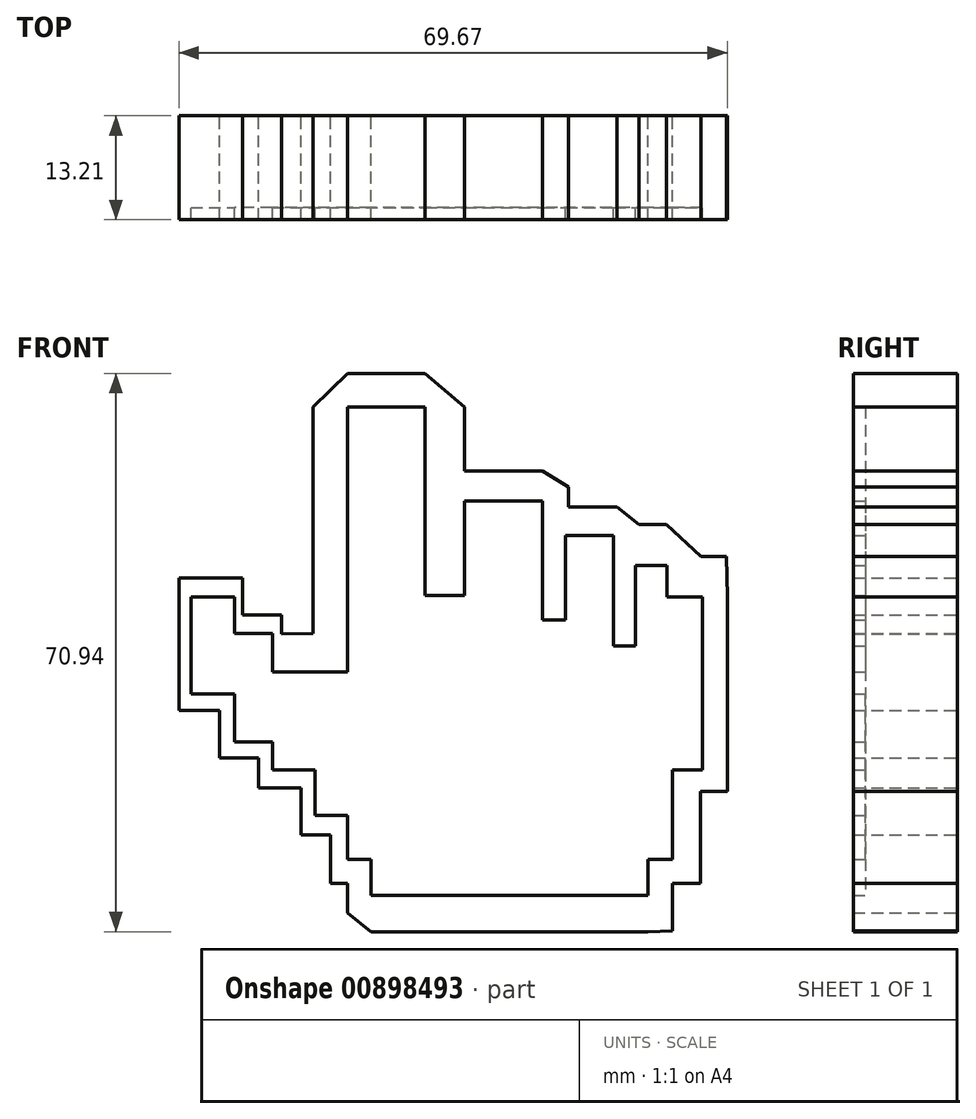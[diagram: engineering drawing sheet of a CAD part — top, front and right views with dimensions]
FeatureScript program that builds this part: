
annotation { "Feature Type Name" : "Feature", "Feature Type Description" : "" }
export const myFeature = defineFeature(function(context is Context, id is Id, definition is map)
    precondition{}
    {
        {
            var Q0;
            Q0=qCreatedBy(makeId("Front.planeOp"),FACE);
            var sketch = newSketch(context, id + "F0", { "sketchPlane" : qUnion([Q0])});
            skLineSegment(sketch, "E0.bottom", {"start": v(0, 0) * mm, "end": v(9.8, 0) * mm});
            skLineSegment(sketch, "E0.top", {"start": v(0, -4.26) * mm, "end": v(9.8, -4.26) * mm});
            skLineSegment(sketch, "E1.left", {"start": v(0, -4.26) * mm, "end": v(0, -28.2) * mm});
            skLineSegment(sketch, "E1.right", {"start": v(-4.42, -4.26) * mm, "end": v(-4.42, -28.2) * mm});
            skLineSegment(sketch, "E2.top", {"start": v(9.8, -28.2) * mm, "end": v(14.84, -28.2) * mm});
            skLineSegment(sketch, "E2.left", {"start": v(9.8, -4.26) * mm, "end": v(9.8, -28.2) * mm});
            skLineSegment(sketch, "E2.right", {"start": v(14.84, -4.26) * mm, "end": v(14.84, -12.42) * mm});
            skLineSegment(sketch, "E3.top", {"start": v(-4.42, -37.93) * mm, "end": v(0, -37.93) * mm});
            skLineSegment(sketch, "E3.left", {"start": v(-4.42, -28.2) * mm, "end": v(-4.42, -33.07) * mm});
            skLineSegment(sketch, "E3.right", {"start": v(0, -28.2) * mm, "end": v(0, -37.93) * mm});
            skLineSegment(sketch, "E4.bottom", {"start": v(14.84, -16.23) * mm, "end": v(24.73, -16.23) * mm});
            skLineSegment(sketch, "E4.top", {"start": v(14.84, -12.42) * mm, "end": v(24.73, -12.42) * mm});
            skLineSegment(sketch, "E5.top", {"start": v(27.68, -20.57) * mm, "end": v(33.76, -20.57) * mm});
            skLineSegment(sketch, "E5.left", {"start": v(24.73, -16.23) * mm, "end": v(24.73, -20.57) * mm});
            skLineSegment(sketch, "E6.top", {"start": v(36.54, -24.4) * mm, "end": v(40.53, -24.4) * mm});
            skLineSegment(sketch, "E6.left", {"start": v(33.76, -20.57) * mm, "end": v(33.76, -24.4) * mm});
            skLineSegment(sketch, "E7.top", {"start": v(40.53, -28.38) * mm, "end": v(45.04, -28.38) * mm});
            skLineSegment(sketch, "E7.left", {"start": v(40.53, -24.4) * mm, "end": v(40.53, -28.38) * mm});
            skLineSegment(sketch, "E8.top", {"start": v(24.73, -31.33) * mm, "end": v(27.68, -31.33) * mm});
            skLineSegment(sketch, "E8.left", {"start": v(24.73, -20.57) * mm, "end": v(24.73, -31.33) * mm});
            skLineSegment(sketch, "E8.right", {"start": v(27.68, -20.57) * mm, "end": v(27.68, -31.33) * mm});
            skLineSegment(sketch, "E9.top", {"start": v(33.76, -34.63) * mm, "end": v(36.54, -34.63) * mm});
            skLineSegment(sketch, "E9.left", {"start": v(33.76, -24.4) * mm, "end": v(33.76, -34.63) * mm});
            skLineSegment(sketch, "E9.right", {"start": v(36.54, -24.4) * mm, "end": v(36.54, -34.63) * mm});
            skLineSegment(sketch, "E10.left", {"start": v(45.04, -28.38) * mm, "end": v(45.04, -50.36) * mm});
            skLineSegment(sketch, "E10.right", {"start": v(48.22, -28.38) * mm, "end": v(48.22, -50.36) * mm});
            skLineSegment(sketch, "E11.bottom", {"start": v(45.04, -50.36) * mm, "end": v(41.22, -50.36) * mm});
            skLineSegment(sketch, "E11.right", {"start": v(41.22, -50.36) * mm, "end": v(41.22, -61.74) * mm});
            skLineSegment(sketch, "E12.bottom", {"start": v(41.22, -61.74) * mm, "end": v(38.15, -61.74) * mm});
            skLineSegment(sketch, "E12.right", {"start": v(38.15, -61.74) * mm, "end": v(38.15, -66.34) * mm});
            skLineSegment(sketch, "E13.bottom", {"start": v(38.15, -66.34) * mm, "end": v(2.98, -66.34) * mm});
            skLineSegment(sketch, "E13.top", {"start": v(38.15, -70.94) * mm, "end": v(2.98, -70.94) * mm});
            skLineSegment(sketch, "E14.top", {"start": v(2.98, -61.74) * mm, "end": v(0, -61.74) * mm});
            skLineSegment(sketch, "E14.left", {"start": v(2.98, -66.34) * mm, "end": v(2.98, -61.74) * mm});
            skLineSegment(sketch, "E15.top", {"start": v(0, -56.2) * mm, "end": v(-4.17, -56.2) * mm});
            skLineSegment(sketch, "E15.left", {"start": v(0, -61.74) * mm, "end": v(0, -56.2) * mm});
            skLineSegment(sketch, "E16.top", {"start": v(-4.17, -50.36) * mm, "end": v(-9.57, -50.36) * mm});
            skLineSegment(sketch, "E16.left", {"start": v(-4.17, -56.2) * mm, "end": v(-4.17, -50.36) * mm});
            skLineSegment(sketch, "E17.top", {"start": v(-9.57, -46.85) * mm, "end": v(-14.39, -46.85) * mm});
            skLineSegment(sketch, "E17.left", {"start": v(-9.57, -50.36) * mm, "end": v(-9.57, -46.85) * mm});
            skLineSegment(sketch, "E18.top", {"start": v(-14.39, -40.72) * mm, "end": v(-19.93, -40.72) * mm});
            skLineSegment(sketch, "E18.left", {"start": v(-14.39, -46.85) * mm, "end": v(-14.39, -40.72) * mm});
            skLineSegment(sketch, "E19.bottom", {"start": v(-19.93, -28.38) * mm, "end": v(-14.39, -28.38) * mm});
            skPoint(sketch, "E20.oppositeSnap0", {"position": v(-4.42, -33.07) * mm});
            skLineSegment(sketch, "E20.top", {"start": v(-14.39, -33.07) * mm, "end": v(-9.57, -33.07) * mm});
            skLineSegment(sketch, "E20.left", {"start": v(-14.39, -28.38) * mm, "end": v(-14.39, -33.07) * mm});
            skLineSegment(sketch, "E21.top", {"start": v(-9.57, -37.93) * mm, "end": v(-4.42, -37.93) * mm});
            skLineSegment(sketch, "E21.left", {"start": v(-9.57, -33.07) * mm, "end": v(-9.57, -37.93) * mm});
            skLineSegment(sketch, "E22", {"start": v(-19.93, -28.38) * mm, "end": v(-19.93, -40.72) * mm});
            skLineSegment(sketch, "E23", {"start": v(-4.42, -4.26) * mm, "end": v(0, 0) * mm});
            skLineSegment(sketch, "E24", {"start": v(9.8, 0) * mm, "end": v(14.84, -4.26) * mm});
            skLineSegment(sketch, "E25.trimOffspring", {"start": v(14.84, -16.23) * mm, "end": v(14.84, -28.2) * mm});
            skLineSegment(sketch, "E26", {"start": v(24.73, -12.42) * mm, "end": v(28.06, -14.42) * mm});
            skLineSegment(sketch, "E27", {"start": v(28.06, -14.42) * mm, "end": v(28.06, -17) * mm});
            skLineSegment(sketch, "E28", {"start": v(28.06, -17) * mm, "end": v(34.2, -17) * mm});
            skLineSegment(sketch, "E29", {"start": v(34.2, -17) * mm, "end": v(37.02, -19.21) * mm});
            skLineSegment(sketch, "E30", {"start": v(37.02, -19.21) * mm, "end": v(40.46, -19.21) * mm});
            skLineSegment(sketch, "E31", {"start": v(40.46, -19.21) * mm, "end": v(44.87, -23.26) * mm});
            skLineSegment(sketch, "E32", {"start": v(44.87, -23.26) * mm, "end": v(48.13, -23.26) * mm});
            skLineSegment(sketch, "E33", {"start": v(48.13, -23.26) * mm, "end": v(48.22, -28.38) * mm});
            skPoint(sketch, "E12.top.end.orphan", {"position": v(38.15, -70.94) * mm});
            skLineSegment(sketch, "E34", {"start": v(48.22, -50.36) * mm, "end": v(48.22, -53.11) * mm});
            skLineSegment(sketch, "E35", {"start": v(48.22, -53.11) * mm, "end": v(44.78, -53.11) * mm});
            skLineSegment(sketch, "E36", {"start": v(44.78, -53.11) * mm, "end": v(44.78, -61.74) * mm});
            skLineSegment(sketch, "E37", {"start": v(44.78, -61.74) * mm, "end": v(44.78, -64.79) * mm});
            skLineSegment(sketch, "E38", {"start": v(44.78, -64.79) * mm, "end": v(41.22, -64.79) * mm});
            skLineSegment(sketch, "E39", {"start": v(41.22, -64.79) * mm, "end": v(41.22, -70.84) * mm});
            skLineSegment(sketch, "E40", {"start": v(41.22, -70.84) * mm, "end": v(38.15, -70.94) * mm});
            skLineSegment(sketch, "E41", {"start": v(2.98, -70.94) * mm, "end": v(0, -68.56) * mm});
            skLineSegment(sketch, "E42", {"start": v(0, -68.56) * mm, "end": v(0, -64.79) * mm});
            skPoint(sketch, "E43.start.orphan", {"position": v(-23.6, -40.72) * mm});
            skPoint(sketch, "E44.end.orphan", {"position": v(-23.6, -28.38) * mm});
            skPoint(sketch, "E19.top.end.orphan", {"position": v(-14.39, -24.23) * mm});
            skLineSegment(sketch, "E45", {"start": v(0, -64.79) * mm, "end": v(-2.17, -64.79) * mm});
            skLineSegment(sketch, "E46", {"start": v(-2.17, -64.79) * mm, "end": v(-2.17, -58.64) * mm});
            skLineSegment(sketch, "E47", {"start": v(-2.17, -58.64) * mm, "end": v(-5.91, -58.64) * mm});
            skLineSegment(sketch, "E48", {"start": v(-5.91, -58.64) * mm, "end": v(-5.91, -52.66) * mm});
            skLineSegment(sketch, "E49", {"start": v(-5.91, -52.66) * mm, "end": v(-11.34, -52.66) * mm});
            skLineSegment(sketch, "E50", {"start": v(-11.34, -52.66) * mm, "end": v(-11.34, -48.84) * mm});
            skLineSegment(sketch, "E51", {"start": v(-11.34, -48.84) * mm, "end": v(-16.27, -48.84) * mm});
            skLineSegment(sketch, "E52", {"start": v(-16.27, -48.84) * mm, "end": v(-16.27, -42.85) * mm});
            skLineSegment(sketch, "E53", {"start": v(-16.27, -42.85) * mm, "end": v(-21.45, -42.85) * mm});
            skLineSegment(sketch, "E54", {"start": v(-21.45, -42.85) * mm, "end": v(-21.45, -26) * mm});
            skLineSegment(sketch, "E55", {"start": v(-21.45, -26) * mm, "end": v(-13.36, -26) * mm});
            skLineSegment(sketch, "E56", {"start": v(-13.36, -26) * mm, "end": v(-13.36, -30.67) * mm});
            skLineSegment(sketch, "E57", {"start": v(-13.36, -30.67) * mm, "end": v(-8.44, -30.67) * mm});
            skLineSegment(sketch, "E58", {"start": v(-8.44, -30.67) * mm, "end": v(-8.44, -33.09) * mm});
            skLineSegment(sketch, "E59", {"start": v(-8.44, -33.09) * mm, "end": v(-4.42, -33.07) * mm});
            skSolve(sketch);
        }
        {
            var Q0;
            Q0=makeQuery(id+"F0.imprint","IMPRINT",FACE,{"disambiguationData":[TD([[makeQuery(id+"F0.imprint","IMPRINT",EDGE,{"derivedFrom":sQuery(id+"F0.wireOp",EDGE,"E0.top")}),-1.0]])]});
            extrude(context, id + "F1", {"entities" : qUnion([Q0]), "depth" : 11.68 * mm, "offsetDistance" : 25.4 * mm});
        }
        {
            var Q0;
            {var subQ1=sQuery(id+"F0.wireOp",EDGE,"E2.bottom");Q0=makeQuery(id+"F0.imprint","IMPRINT",FACE,{"disambiguationData":[TD([[makeQuery(id+"F0.imprint","IMPRINT",EDGE,{"derivedFrom":subQ1}),-1.0]])]});}
            var Q1;
            Q1=makeQuery(id+"F0.imprint","IMPRINT",FACE,{"disambiguationData":[TD([[makeQuery(id+"F0.imprint","IMPRINT",EDGE,{"derivedFrom":sQuery(id+"F0.wireOp",EDGE,"E8.bottom")}),-1.0]])]});
            var Q2;
            Q2=makeQuery(id+"F0.imprint","IMPRINT",FACE,{"disambiguationData":[TD([[makeQuery(id+"F0.imprint","IMPRINT",EDGE,{"derivedFrom":sQuery(id+"F0.wireOp",EDGE,"E9.bottom")}),-1.0]])]});
            var Q3;
            Q3=makeQuery(id+"F0.imprint","IMPRINT",FACE,{"disambiguationData":[TD([[makeQuery(id+"F0.imprint","IMPRINT",EDGE,{"derivedFrom":sQuery(id+"F0.wireOp",EDGE,"E19.bottom")}),1.0]])]});
            extrude(context, id + "F2", {"entities" : qUnion([Q0, Q1, Q2, Q3]), "operationType" : NewBodyOperationType.ADD, "depth" : 13.2 * mm, "offsetDistance" : 25.4 * mm});
        }
    });
